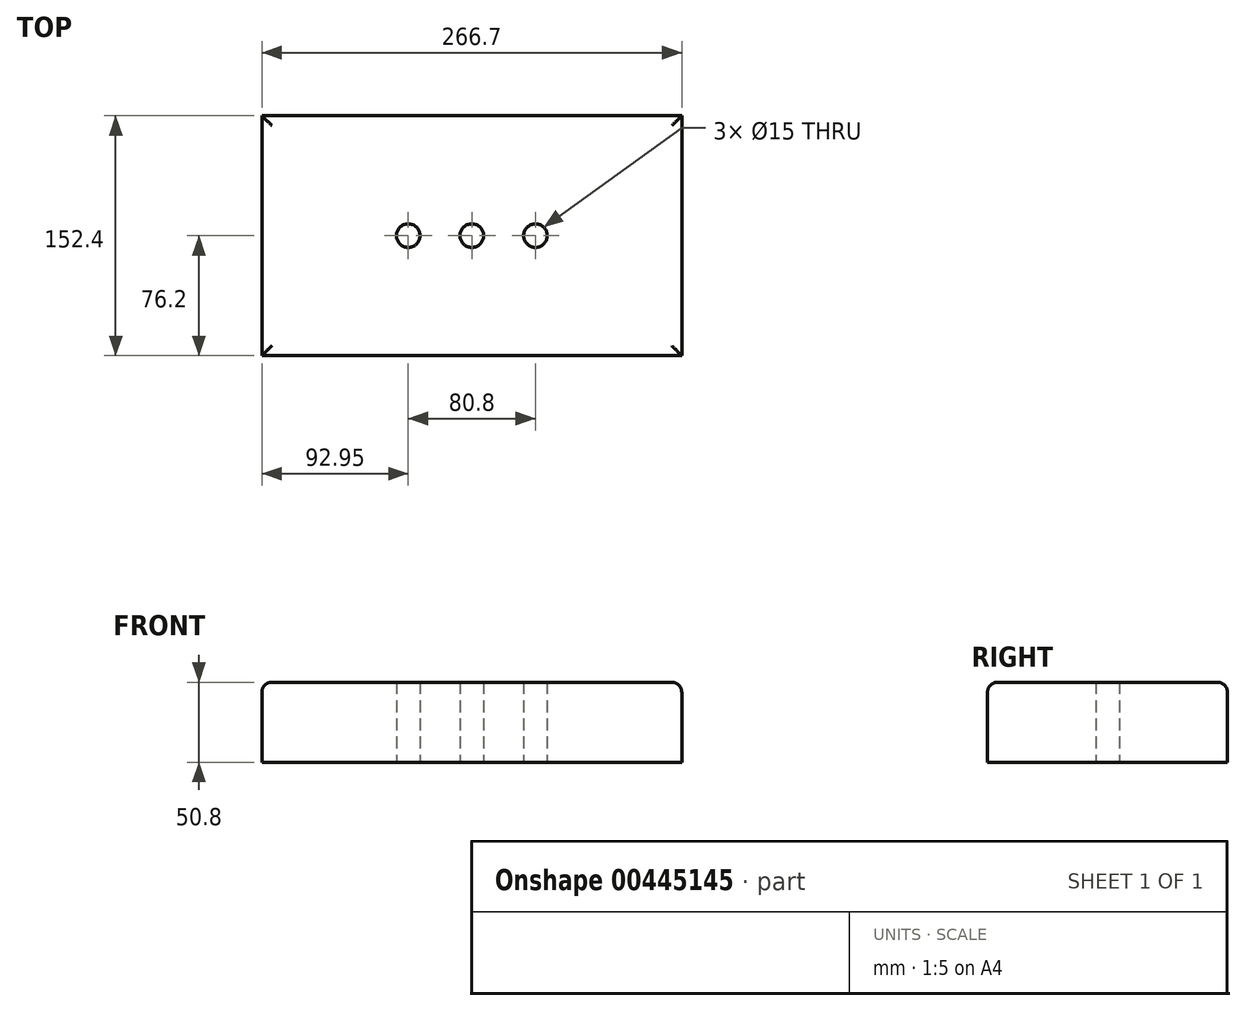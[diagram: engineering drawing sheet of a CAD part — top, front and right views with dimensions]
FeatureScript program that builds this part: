
annotation { "Feature Type Name" : "Feature", "Feature Type Description" : "" }
export const myFeature = defineFeature(function(context is Context, id is Id, definition is map)
    precondition{}
    {
        {
            var Q0;
            Q0=qCreatedBy(makeId("Top.planeOp"),FACE);
            var sketch = newSketch(context, id + "F0", { "sketchPlane" : qUnion([Q0])});
            skLineSegment(sketch, "E0.bottom", {"start": v(133.35, 76.2) * mm, "end": v(-133.35, 76.2) * mm});
            skLineSegment(sketch, "E0.top", {"start": v(133.35, -76.2) * mm, "end": v(-133.35, -76.2) * mm});
            skLineSegment(sketch, "E0.left", {"start": v(133.35, 76.2) * mm, "end": v(133.35, -76.2) * mm});
            skLineSegment(sketch, "E0.right", {"start": v(-133.35, 76.2) * mm, "end": v(-133.35, -76.2) * mm});
            skPoint(sketch, "E0.middle", {"position": v(0, 0) * mm});
            skCircle(sketch, "E1", {"center": v(0, 0) * mm, "radius": 7.5 * mm});
            skPoint(sketch, "E2", {"position": v(-40.4, 0) * mm});
            skPoint(sketch, "E3", {"position": v(40.4, 0) * mm});
            skCircle(sketch, "E4", {"center": v(-40.4, 0) * mm, "radius": 7.5 * mm});
            skCircle(sketch, "E5", {"center": v(40.4, 0) * mm, "radius": 7.5 * mm});
            skLineSegment(sketch, "E6", {"start": v(-32.9, 0) * mm, "end": v(-7.5, 0) * mm});
            skLineSegment(sketch, "E7", {"start": v(7.5, 0) * mm, "end": v(32.9, 0) * mm});
            skSolve(sketch);
        }
        {
            var Q0;
            Q0=makeQuery(id+"F0.imprint","IMPRINT",FACE,{"disambiguationData":[TD([[makeQuery(id+"F0.imprint","IMPRINT",EDGE,{"derivedFrom":sQuery(id+"F0.wireOp",EDGE,"E0.bottom")}),1.0]])]});
            extrude(context, id + "F1", {"entities" : qUnion([Q0]), "depth" : 50.8 * mm});
        }
        {
            var Q0;
            Q0=makeQuery(id+"F1.opExtrude","CAP_EDGE",EDGE,{"disambiguationData":[OSD([sQuery(id+"F0.wireOp",EDGE,"E0.bottom")])],"isStart":false});
            var Q1;
            Q1=makeQuery(id+"F1.opExtrude","CAP_EDGE",EDGE,{"disambiguationData":[OSD([sQuery(id+"F0.wireOp",EDGE,"E0.right")])],"isStart":false});
            var Q2;
            Q2=makeQuery(id+"F1.opExtrude","CAP_EDGE",EDGE,{"disambiguationData":[OSD([sQuery(id+"F0.wireOp",EDGE,"E0.top")])],"isStart":false});
            var Q3;
            Q3=makeQuery(id+"F1.opExtrude","CAP_EDGE",EDGE,{"disambiguationData":[OSD([sQuery(id+"F0.wireOp",EDGE,"E0.left")])],"isStart":false});
            fillet(context, id + "F2", {"entities" : qUnion([Q0, Q1, Q2, Q3]), "radius" : 6.35 * mm, "tangentPropagation" : true, "allowEdgeOverflow" : false});
        }
    });
